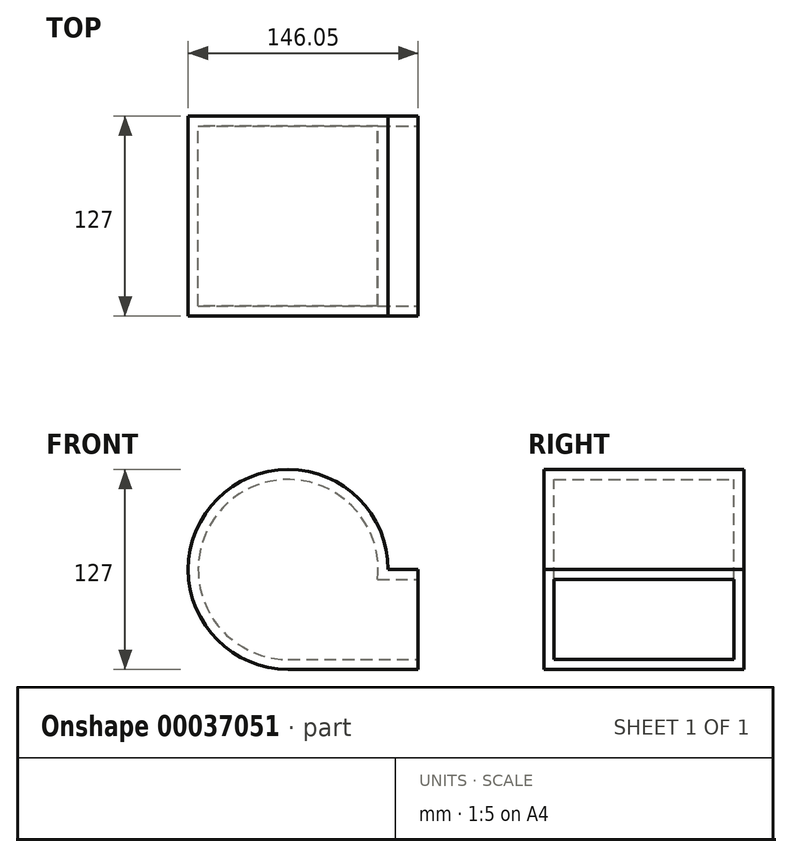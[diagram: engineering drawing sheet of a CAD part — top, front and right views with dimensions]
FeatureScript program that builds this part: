
annotation { "Feature Type Name" : "Feature", "Feature Type Description" : "" }
export const myFeature = defineFeature(function(context is Context, id is Id, definition is map)
    precondition{}
    {
        {
            var Q0;
            Q0=qCreatedBy(makeId("Front.planeOp"),FACE);
            var sketch = newSketch(context, id + "F0", { "sketchPlane" : qUnion([Q0])});
            skLineSegment(sketch, "E0.bottom", {"start": v(-82.55, 0) * mm, "end": v(0, 0) * mm});
            skLineSegment(sketch, "E0.top", {"start": v(-19.05, 63.5) * mm, "end": v(0, 63.5) * mm});
            skLineSegment(sketch, "E0.right", {"start": v(0, 0) * mm, "end": v(0, 63.5) * mm});
            skArc(sketch, "E1", {"start": v(-19.05, 63.5) * mm, "mid": v(-127.45, 108.4) * mm, "end": v(-82.55, 0) * mm});
            skSolve(sketch);
        }
        {
            var Q0;
            Q0=makeQuery(id+"F0.imprint","IMPRINT",FACE,{"disambiguationData":[TD([[makeQuery(id+"F0.imprint","IMPRINT",EDGE,{"derivedFrom":sQuery(id+"F0.wireOp",EDGE,"E0.bottom")}),1.0]])]});
            extrude(context, id + "F1", {"entities" : qUnion([Q0]), "depth" : 127 * mm});
        }
        {
            var Q0;
            Q0=makeQuery(id+"F1.opExtrude","SWEPT_FACE",FACE,{"disambiguationData":[OSD([sQuery(id+"F0.wireOp",EDGE,"E0.right")])]});
            shell(context, id + "F2", {"entities" : qUnion([Q0]), "thickness" : 6.35 * mm});
        }
    });
